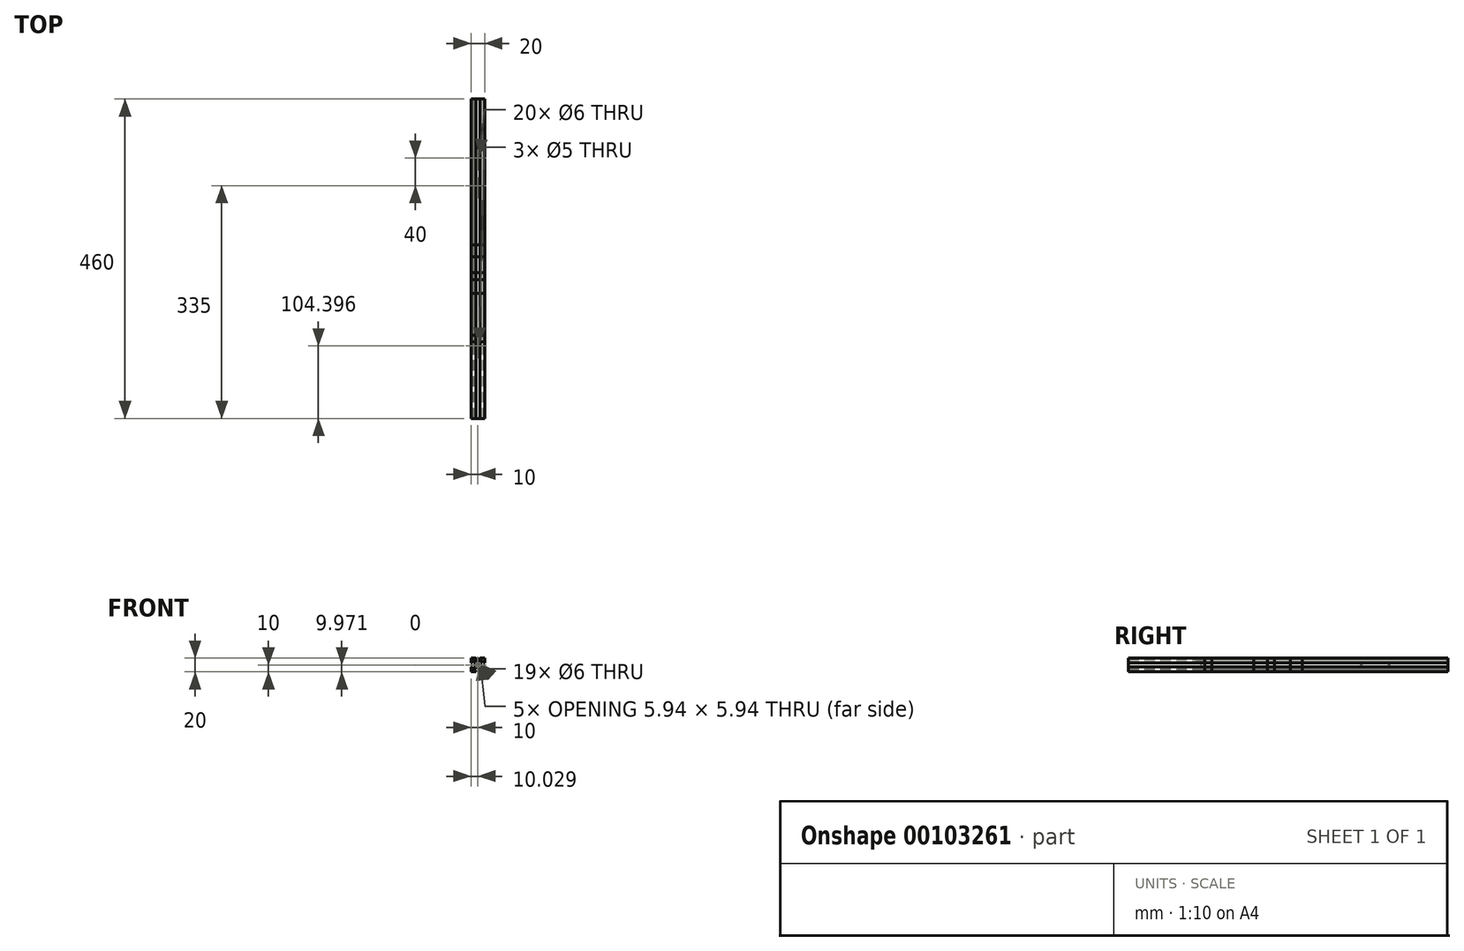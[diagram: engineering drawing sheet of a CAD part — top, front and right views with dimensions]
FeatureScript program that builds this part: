
annotation { "Feature Type Name" : "Feature", "Feature Type Description" : "" }
export const myFeature = defineFeature(function(context is Context, id is Id, definition is map)
    precondition{}
    {
        {
            var Q0;
            Q0=qCreatedBy(makeId("Front.planeOp"),FACE);
            var sketch = newSketch(context, id + "F0", { "sketchPlane" : qUnion([Q0])});
            skCircle(sketch, "E0", {"center": v(0, 0) * mm, "radius": 3 * mm});
            skLineSegment(sketch, "E1.left", {"start": v(3, 8) * mm, "end": v(3, 10) * mm});
            skLineSegment(sketch, "E2", {"start": v(3, 10) * mm, "end": v(10, 10) * mm});
            skLineSegment(sketch, "E3", {"start": v(3, 8) * mm, "end": v(5.19, 8) * mm});
            skLineSegment(sketch, "E4", {"start": v(0, 4) * mm, "end": v(1.21, 4) * mm});
            skLineSegment(sketch, "E5", {"start": v(0, 0) * mm, "end": v(10, 10) * mm, "construction": true});
            skArc(sketch, "E6", {"start": v(1.21, 4) * mm, "mid": v(4.03, 5.17) * mm, "end": v(5.19, 8) * mm});
            skLineSegment(sketch, "E7.MirrorCS", {"start": v(10, 3) * mm, "end": v(10, 10) * mm});
            skLineSegment(sketch, "E8.MirrorCS", {"start": v(8, 3) * mm, "end": v(10, 3) * mm});
            skLineSegment(sketch, "E9.MirrorCS", {"start": v(8, 3) * mm, "end": v(8, 5.19) * mm});
            skArc(sketch, "E10.MirrorCS", {"start": v(4, 1.21) * mm, "mid": v(5.17, 4.03) * mm, "end": v(8, 5.19) * mm});
            skLineSegment(sketch, "E11.MirrorCS", {"start": v(4, 0) * mm, "end": v(4, 1.21) * mm});
            skLineSegment(sketch, "E12.MirrorCS", {"start": v(-3, 8) * mm, "end": v(-3, 10) * mm});
            skLineSegment(sketch, "E13.MirrorCS", {"start": v(-3, 10) * mm, "end": v(-10, 10) * mm});
            skArc(sketch, "E14.MirrorCS", {"start": v(-4, 1.21) * mm, "mid": v(-5.17, 4.03) * mm, "end": v(-8, 5.19) * mm});
            skLineSegment(sketch, "E15.MirrorCS", {"start": v(-4, 0) * mm, "end": v(-4, 1.21) * mm});
            skLineSegment(sketch, "E16.MirrorCS", {"start": v(0, 4) * mm, "end": v(-1.21, 4) * mm});
            skLineSegment(sketch, "E17.MirrorCS", {"start": v(0, 0) * mm, "end": v(-10, 10) * mm, "construction": true});
            skLineSegment(sketch, "E18.MirrorCS", {"start": v(-8, 3) * mm, "end": v(-10, 3) * mm});
            skLineSegment(sketch, "E19.MirrorCS", {"start": v(-8, 3) * mm, "end": v(-8, 5.19) * mm});
            skLineSegment(sketch, "E20.MirrorCS", {"start": v(-10, 3) * mm, "end": v(-10, 10) * mm});
            skLineSegment(sketch, "E21.MirrorCS", {"start": v(-3, 8) * mm, "end": v(-5.19, 8) * mm});
            skArc(sketch, "E22.MirrorCS", {"start": v(-1.21, 4) * mm, "mid": v(-4.03, 5.17) * mm, "end": v(-5.19, 8) * mm});
            skLineSegment(sketch, "E23.MirrorCS", {"start": v(0, -4) * mm, "end": v(-1.21, -4) * mm});
            skLineSegment(sketch, "E24.MirrorCS", {"start": v(-8, -3) * mm, "end": v(-10, -3) * mm});
            skLineSegment(sketch, "E25.MirrorCS", {"start": v(-10, -3) * mm, "end": v(-10, -10) * mm});
            skArc(sketch, "E26.MirrorCS", {"start": v(-1.21, -4) * mm, "mid": v(-4.03, -5.17) * mm, "end": v(-5.19, -8) * mm});
            skLineSegment(sketch, "E27.MirrorCS", {"start": v(-3, -8) * mm, "end": v(-3, -10) * mm});
            skLineSegment(sketch, "E28.MirrorCS", {"start": v(4, 0) * mm, "end": v(4, -1.21) * mm});
            skArc(sketch, "E29.MirrorCS", {"start": v(4, -1.21) * mm, "mid": v(5.17, -4.03) * mm, "end": v(8, -5.19) * mm});
            skLineSegment(sketch, "E30.MirrorCS", {"start": v(8, -3) * mm, "end": v(8, -5.19) * mm});
            skLineSegment(sketch, "E31.MirrorCS", {"start": v(8, -3) * mm, "end": v(10, -3) * mm});
            skLineSegment(sketch, "E32.MirrorCS", {"start": v(10, -3) * mm, "end": v(10, -10) * mm});
            skArc(sketch, "E33.MirrorCS", {"start": v(1.21, -4) * mm, "mid": v(4.03, -5.17) * mm, "end": v(5.19, -8) * mm});
            skLineSegment(sketch, "E34.MirrorCS", {"start": v(0, 0) * mm, "end": v(10, -10) * mm, "construction": true});
            skLineSegment(sketch, "E35.MirrorCS", {"start": v(0, -4) * mm, "end": v(1.21, -4) * mm});
            skLineSegment(sketch, "E36.MirrorCS", {"start": v(3, -8) * mm, "end": v(5.19, -8) * mm});
            skLineSegment(sketch, "E37.MirrorCS", {"start": v(3, -8) * mm, "end": v(3, -10) * mm});
            skLineSegment(sketch, "E38.MirrorCS", {"start": v(0, 0) * mm, "end": v(-10, -10) * mm, "construction": true});
            skArc(sketch, "E39.MirrorCS", {"start": v(-4, -1.21) * mm, "mid": v(-5.17, -4.03) * mm, "end": v(-8, -5.19) * mm});
            skLineSegment(sketch, "E40.MirrorCS", {"start": v(-3, -10) * mm, "end": v(-10, -10) * mm});
            skLineSegment(sketch, "E41.MirrorCS", {"start": v(3, -10) * mm, "end": v(10, -10) * mm});
            skLineSegment(sketch, "E42.MirrorCS", {"start": v(-3, -8) * mm, "end": v(-5.19, -8) * mm});
            skLineSegment(sketch, "E43.MirrorCS", {"start": v(-4, 0) * mm, "end": v(-4, -1.21) * mm});
            skLineSegment(sketch, "E44.MirrorCS", {"start": v(-8, -3) * mm, "end": v(-8, -5.19) * mm});
            skSolve(sketch);
        }
        {
            var Q0;
            Q0=makeQuery(id+"F0.imprint","IMPRINT",FACE,{"disambiguationData":[TD([[makeQuery(id+"F0.imprint","IMPRINT",EDGE,{"derivedFrom":sQuery(id+"F0.wireOp",EDGE,"E0")}),-1.0]])]});
            extrude(context, id + "F1", {"entities" : qUnion([Q0]), "depth" : 350 * mm});
        }
        {
            var Q0;
            Q0 = qSketchRegion(id + "F0", true);
            extrude(context, id + "F2", {"entities" : qUnion([Q0]), "depth" : 260 * mm});
        }
        {
            var Q0;
            Q0 = qSketchRegion(id + "F0", true);
            extrude(context, id + "F3", {"entities" : qUnion([Q0]), "depth" : 460 * mm});
        }
        {
            var Q0;
            Q0 = qSketchRegion(id + "F0", true);
            extrude(context, id + "F4", {"entities" : qUnion([Q0]), "depth" : 280 * mm});
        }
        {
            var Q0;
            Q0 = qSketchRegion(id + "F0", true);
            extrude(context, id + "F5", {"entities" : qUnion([Q0]), "depth" : 210 * mm});
        }
        {
            var Q0;
            Q0=makeQuery(id+"F5.opExtrude","SWEPT_FACE",FACE,{"disambiguationData":[OSD([sQuery(id+"F0.wireOp",EDGE,"E2")])]});
            var sketch = newSketch(context, id + "F6", { "sketchPlane" : qUnion([Q0])});
            skLineSegment(sketch, "E45", {"start": v(0, -105) * mm, "end": v(10, -105) * mm, "construction": true});
            skLineSegment(sketch, "E46", {"start": v(0, -105) * mm, "end": v(0, 26.92) * mm, "construction": true});
            skCircle(sketch, "E47", {"center": v(0, -85) * mm, "radius": 3 * mm});
            skCircle(sketch, "E48.MirrorC", {"center": v(0, -125) * mm, "radius": 3 * mm});
            skSolve(sketch);
        }
        {
            var Q0;
            Q0 = qSketchRegion(id + "F6", true);
            extrude(context, id + "F7", {"entities" : qUnion([Q0]), "operationType" : NewBodyOperationType.REMOVE, "endBound" : BoundingType.THROUGH_ALL, "oppositeDirection" : true, "depth" : 25 * mm});
        }
        {
            var Q0;
            Q0 = qSketchRegion(id + "F0", true);
            extrude(context, id + "F8", {"entities" : qUnion([Q0]), "depth" : 250 * mm});
        }
        {
            var Q0;
            Q0=makeQuery(id+"F1.opExtrude","CAP_FACE",FACE,{"disambiguationData":[OSD([sQuery(id+"F0.wireOp",EDGE,"E0"),sQuery(id+"F0.wireOp",EDGE,"E1.left"),sQuery(id+"F0.wireOp",EDGE,"E2"),sQuery(id+"F0.wireOp",EDGE,"E3"),sQuery(id+"F0.wireOp",EDGE,"E4"),sQuery(id+"F0.wireOp",EDGE,"E6"),sQuery(id+"F0.wireOp",EDGE,"E7.MirrorCS"),sQuery(id+"F0.wireOp",EDGE,"E8.MirrorCS"),sQuery(id+"F0.wireOp",EDGE,"E9.MirrorCS"),sQuery(id+"F0.wireOp",EDGE,"E10.MirrorCS"),sQuery(id+"F0.wireOp",EDGE,"E11.MirrorCS"),sQuery(id+"F0.wireOp",EDGE,"E12.MirrorCS"),sQuery(id+"F0.wireOp",EDGE,"E13.MirrorCS"),sQuery(id+"F0.wireOp",EDGE,"E14.MirrorCS"),sQuery(id+"F0.wireOp",EDGE,"E15.MirrorCS"),sQuery(id+"F0.wireOp",EDGE,"E16.MirrorCS"),sQuery(id+"F0.wireOp",EDGE,"E18.MirrorCS"),sQuery(id+"F0.wireOp",EDGE,"E19.MirrorCS"),sQuery(id+"F0.wireOp",EDGE,"E20.MirrorCS"),sQuery(id+"F0.wireOp",EDGE,"E21.MirrorCS"),sQuery(id+"F0.wireOp",EDGE,"E22.MirrorCS"),sQuery(id+"F0.wireOp",EDGE,"E23.MirrorCS"),sQuery(id+"F0.wireOp",EDGE,"E24.MirrorCS"),sQuery(id+"F0.wireOp",EDGE,"E25.MirrorCS"),sQuery(id+"F0.wireOp",EDGE,"E26.MirrorCS"),sQuery(id+"F0.wireOp",EDGE,"E27.MirrorCS"),sQuery(id+"F0.wireOp",EDGE,"E28.MirrorCS"),sQuery(id+"F0.wireOp",EDGE,"E29.MirrorCS"),sQuery(id+"F0.wireOp",EDGE,"E30.MirrorCS"),sQuery(id+"F0.wireOp",EDGE,"E31.MirrorCS"),sQuery(id+"F0.wireOp",EDGE,"E32.MirrorCS"),sQuery(id+"F0.wireOp",EDGE,"E33.MirrorCS"),sQuery(id+"F0.wireOp",EDGE,"E35.MirrorCS"),sQuery(id+"F0.wireOp",EDGE,"E36.MirrorCS"),sQuery(id+"F0.wireOp",EDGE,"E37.MirrorCS"),sQuery(id+"F0.wireOp",EDGE,"E39.MirrorCS"),sQuery(id+"F0.wireOp",EDGE,"E40.MirrorCS"),sQuery(id+"F0.wireOp",EDGE,"E41.MirrorCS"),sQuery(id+"F0.wireOp",EDGE,"E42.MirrorCS"),sQuery(id+"F0.wireOp",EDGE,"E43.MirrorCS"),sQuery(id+"F0.wireOp",EDGE,"E44.MirrorCS")])],"isStart":false});
            var sketch = newSketch(context, id + "F9", { "sketchPlane" : qUnion([Q0])});
            skLineSegment(sketch, "E49", {"start": v(0, 8.7) * mm, "end": v(3, 8.7) * mm});
            skLineSegment(sketch, "E50", {"start": v(3, 8.7) * mm, "end": v(3, 8) * mm});
            skLineSegment(sketch, "E51", {"start": v(3, 8) * mm, "end": v(5.19, 8) * mm});
            skArc(sketch, "E52.0", {"start": v(4.65, 5.97) * mm, "mid": v(5.05, 6.95) * mm, "end": v(5.19, 8) * mm});
            skLineSegment(sketch, "E53", {"start": v(0, 5.97) * mm, "end": v(4.65, 5.97) * mm});
            skPoint(sketch, "E54.orphan", {"position": v(1.21, 4) * mm});
            skLineSegment(sketch, "E55.MirrorCS", {"start": v(0, 8.7) * mm, "end": v(-3, 8.7) * mm});
            skLineSegment(sketch, "E56.MirrorCS", {"start": v(-3, 8.7) * mm, "end": v(-3, 8) * mm});
            skLineSegment(sketch, "E57.MirrorCS", {"start": v(-3, 8) * mm, "end": v(-5.19, 8) * mm});
            skArc(sketch, "E58.MirrorCS", {"start": v(-4.65, 5.97) * mm, "mid": v(-5.05, 6.95) * mm, "end": v(-5.19, 8) * mm});
            skLineSegment(sketch, "E59.MirrorCS", {"start": v(0, 5.97) * mm, "end": v(-4.65, 5.97) * mm});
            skSolve(sketch);
        }
        {
            var Q0;
            Q0 = qSketchRegion(id + "F9", true);
            extrude(context, id + "F10", {"entities" : qUnion([Q0]), "depth" : 12 * mm});
        }
        {
            var Q0;
            Q0=makeQuery(id+"F10.opExtrude","SWEPT_FACE",FACE,{"disambiguationData":[OSD([sQuery(id+"F9.wireOp",EDGE,"E49"),sQuery(id+"F9.wireOp",EDGE,"E55.MirrorCS")])]});
            var sketch = newSketch(context, id + "F11", { "sketchPlane" : qUnion([Q0])});
            skCircle(sketch, "E60", {"center": v(0, -355.6) * mm, "radius": 2.5 * mm});
            skPoint(sketch, "E60.centerSnap0", {"position": v(0, -362) * mm});
            skSolve(sketch);
        }
        {
            var Q0;
            Q0 = qSketchRegion(id + "F11", true);
            extrude(context, id + "F12", {"entities" : qUnion([Q0]), "operationType" : NewBodyOperationType.REMOVE, "endBound" : BoundingType.THROUGH_ALL, "oppositeDirection" : true, "depth" : 25 * mm});
        }
        {
            var Q0;
            Q0 = qSketchRegion(id + "F0", true);
            extrude(context, id + "F13", {"entities" : qUnion([Q0]), "depth" : 460 * mm});
        }
        {
            var Q0;
            Q0 = qSketchRegion(id + "F0", true);
            extrude(context, id + "F14", {"entities" : qUnion([Q0]), "depth" : 227 * mm});
        }
        {
            var Q0;
            Q0 = qSketchRegion(id + "F0", true);
            extrude(context, id + "F15", {"entities" : qUnion([Q0]), "depth" : 340 * mm});
        }
    });
